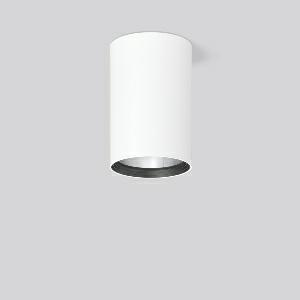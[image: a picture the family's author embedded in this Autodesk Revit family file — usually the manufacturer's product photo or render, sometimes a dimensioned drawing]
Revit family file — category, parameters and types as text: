
# Revit family: heledon_maxi_a_931216_002_3_6c74
name_source: partatom
category: Lighting Fixtures
units: mm (PartAtom-declared; Revit-internal decimal feet)

## family parameters
Cut with Voids When Loaded = No
Host = Face
Light Source = No
Part Type = Normal
Room Calculation Point = No
Round Connector Dimension = Use Diameter
Shared = No

## types (1)
- HELEDON maxi A (1 x LED Modul 935, 3300 lm, 3500)
    Apparent Load = 25 VA
    Approval mark = CE
    CIE Flux Codes = 100 100 100 100 100
    Color Rendering = 92
    Color Temperature = 3500
    Default Elevation = 1800 mm
    Description = Series: HELEDON maxi
Cylindrical surface-mounted downlight. Housing: die-cast aluminium, powder-coated. Internal ceiling frame polycarbonate with bayonet mounting. Black plastic ring and recessed LED to prevent glare from the side. Optical assembly with reflector made of MIRO-Silver with 98% total light reflection for outstanding efficiency - can be changed without tools. Best colour rendering index Ra>90. Suitable for Ceiling mounting. Easy installation with a separate ceiling frame with bayonet mounting and plug connection. Driver integrated. Connected via plug-in connector. High quality converter without flickering and stroboscopic effect. The following accessories can be mounted without use of tools: interchangeable lenses, decorative glasses, honeycomb louvre, clear and frosted diffusers, white interchangeable plastic ring. 
Colour: traffic white, matt (RAL 9016)
Diameter: 123 mm
Height: 183 mm
Lamp: LED
Socket: without socket
Colour temperature: 3500K
Colour rendering index (CRI): 92
System power: 25 W
Rated luminous flux: 3300 lm
Luminous efficiency: 132 lm/W
Control gear: Regulated power supply
Protection class: I
Type of protection: IP 20
    Height = 183 mm
    Lamp = 1 x LED Modul 935
    Lamp Light Flux = 3300 lm
    Lamp count = 1
    Length = 123 mm
    Lifetime = 50000 h
    Luminous efficacy = 132 lm/W
    Manufacturer = RZB
    ModVariant = No
    Model = 931216.002.3
    Mounting Place = Ceiling
    Mounting Type = Surface mounted
    Number of Poles = 1
    OnlyDefault = Yes
    Power Factor = 1
    Product Name = HELEDON maxi A
    Product group = Surface mounted downlights
    ProductGroupID = 302
    Protection Class = Protection class I
    Protection Degree = IP 20
    RLX_Detail_Level = 1
    RLX_Emergency_Light_Flux = 0 lm
    RLX_Emergency_Type = 0
    RLX_Emergency_Type_DB = No
    RlxData = <blob elided: 96853 chars, md5=40a43992>
    Socket = socket
    Standby Power = 0 W
    System Light Flux = 3300 lm
    System Power = 25 W
    Type Comments = Product without accessories
    Type Image = 931192.002.jpg
    URL = http://relux.com
    VarID = ---
    Voltage = 230 V
    Voltage Range = 220-240 V
    Weight = 0.00 kg
    Width = 0 mm  [stored 0 ft]

note: [stored X ft] marks values corroborated as IEEE doubles in the binary element streams (Revit-internal decimal feet)

## geometry (parser evidence)
native form markers: Blend x4, Sweep x11
no freeform markers — native parametric forms only
